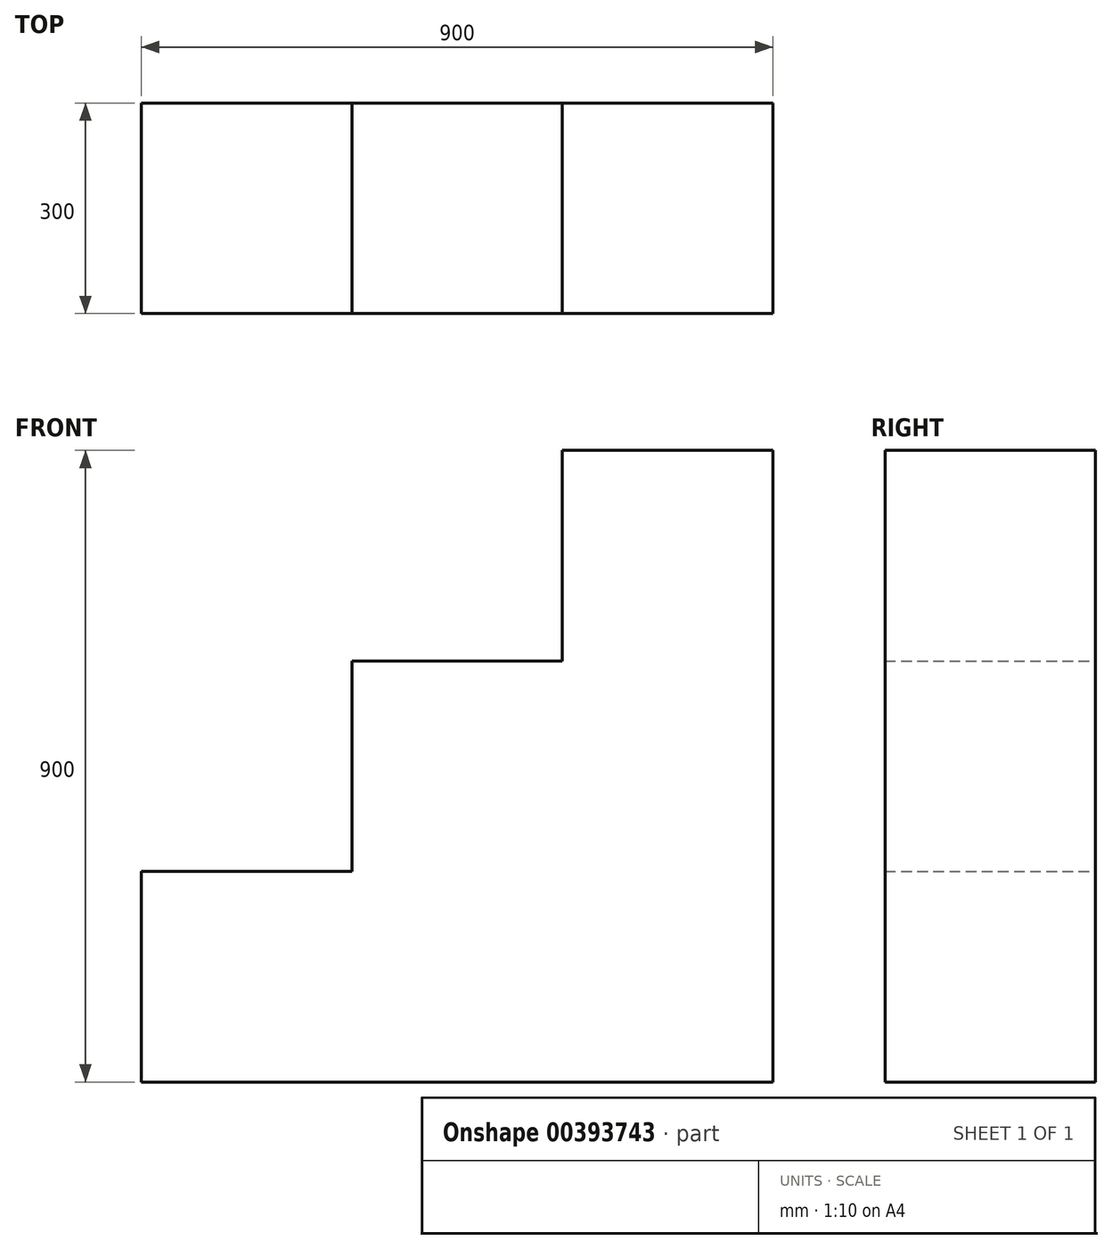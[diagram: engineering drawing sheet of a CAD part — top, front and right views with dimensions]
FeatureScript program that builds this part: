
annotation { "Feature Type Name" : "Feature", "Feature Type Description" : "" }
export const myFeature = defineFeature(function(context is Context, id is Id, definition is map)
    precondition{}
    {
        {
            var Q0;
            Q0=qCreatedBy(makeId("Front.planeOp"),FACE);
            var sketch = newSketch(context, id + "F0", { "sketchPlane" : qUnion([Q0])});
            skLineSegment(sketch, "E0.bottom", {"start": v(450, 450) * mm, "end": v(150, 450) * mm});
            skLineSegment(sketch, "E0.top", {"start": v(450, -450) * mm, "end": v(-450, -450) * mm});
            skLineSegment(sketch, "E0.left", {"start": v(450, 450) * mm, "end": v(450, -450) * mm});
            skLineSegment(sketch, "E0.right", {"start": v(-450, -150) * mm, "end": v(-450, -450) * mm});
            skPoint(sketch, "E0.middle", {"position": v(0, 0) * mm});
            skLineSegment(sketch, "E1", {"start": v(150, 450) * mm, "end": v(150, 150) * mm});
            skLineSegment(sketch, "E2", {"start": v(150, 150) * mm, "end": v(-150, 150) * mm});
            skLineSegment(sketch, "E3", {"start": v(-150, 150) * mm, "end": v(-150, -150) * mm});
            skLineSegment(sketch, "E4", {"start": v(-150, -150) * mm, "end": v(-450, -150) * mm});
            skPoint(sketch, "E5.orphan", {"position": v(-450, 450) * mm});
            skSolve(sketch);
        }
        {
            var Q0;
            Q0 = qSketchRegion(id + "F0", true);
            extrude(context, id + "F1", {"entities" : qUnion([Q0]), "depth" : 300 * mm});
        }
    });
